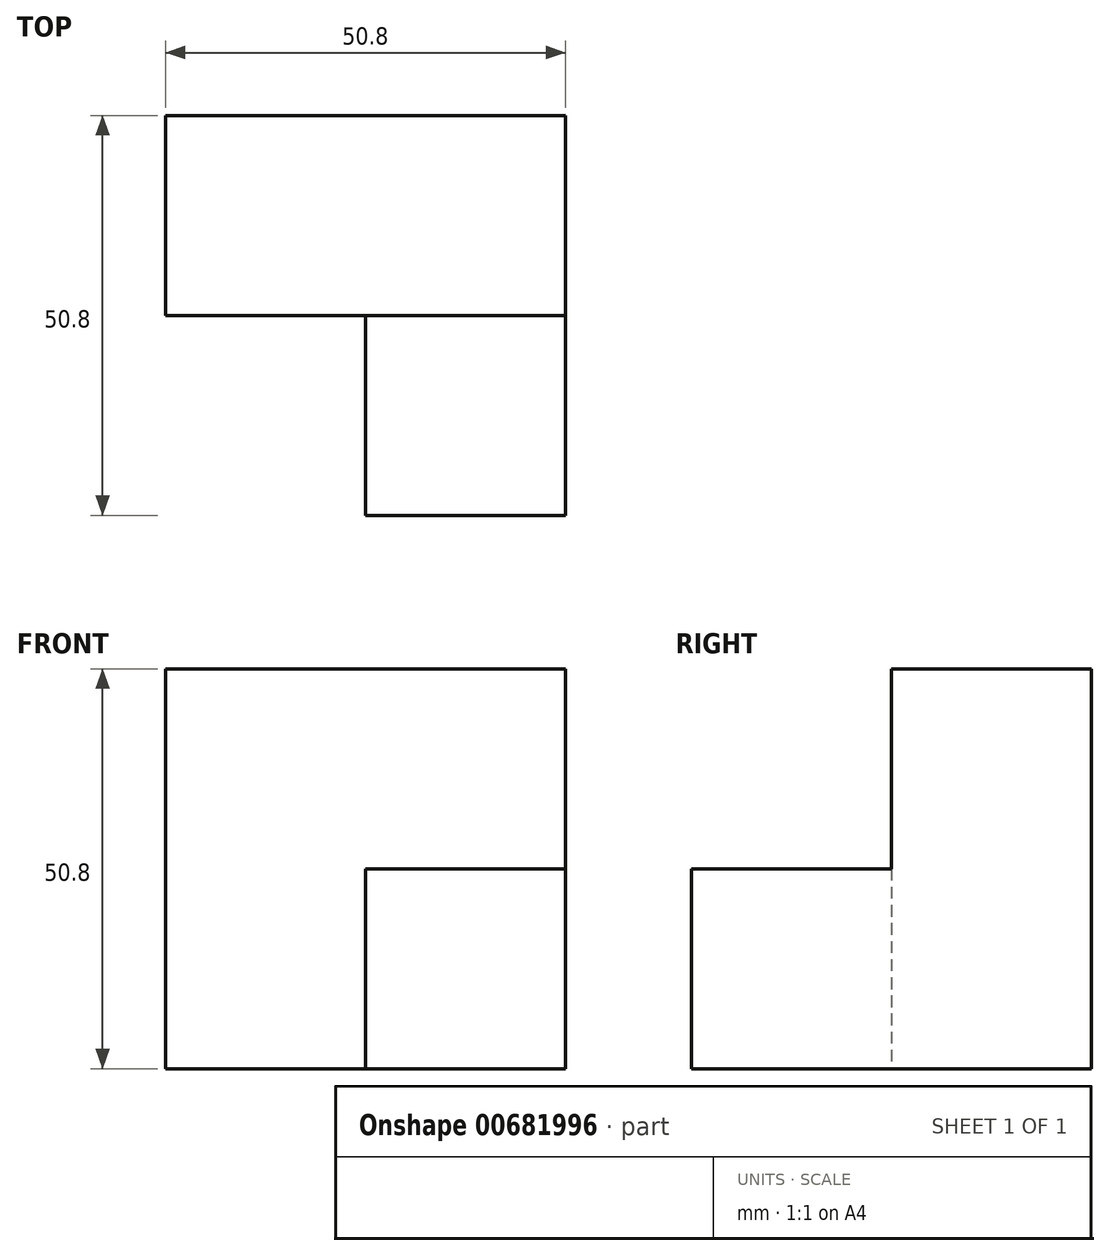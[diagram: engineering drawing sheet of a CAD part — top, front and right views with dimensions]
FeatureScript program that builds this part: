
annotation { "Feature Type Name" : "Feature", "Feature Type Description" : "" }
export const myFeature = defineFeature(function(context is Context, id is Id, definition is map)
    precondition{}
    {
        {
            var Q0;
            Q0=qCreatedBy(makeId("Front.planeOp"),FACE);
            var sketch = newSketch(context, id + "F0", { "sketchPlane" : qUnion([Q0])});
            skLineSegment(sketch, "E0", {"start": v(0, 0) * mm, "end": v(0, 50.8) * mm});
            skLineSegment(sketch, "E1", {"start": v(0, 50.8) * mm, "end": v(-50.8, 50.8) * mm});
            skLineSegment(sketch, "E2", {"start": v(-50.8, 50.8) * mm, "end": v(-50.8, 0) * mm});
            skLineSegment(sketch, "E3", {"start": v(-50.8, 0) * mm, "end": v(0, 0) * mm});
            skSolve(sketch);
        }
        {
            var Q0;
            Q0=makeQuery(id+"F0.imprint","IMPRINT",FACE,{"disambiguationData":[TD([[makeQuery(id+"F0.imprint","IMPRINT",EDGE,{"derivedFrom":sQuery(id+"F0.wireOp",EDGE,"E0")}),1.0]])]});
            extrude(context, id + "F1", {"entities" : qUnion([Q0]), "depth" : 25.4 * mm, "offsetDistance" : 25.4 * mm});
        }
        {
            var Q0;
            Q0=makeQuery(id+"F1.opExtrude","CAP_FACE",FACE,{"disambiguationData":[OSD([sQuery(id+"F0.wireOp",EDGE,"E0"),sQuery(id+"F0.wireOp",EDGE,"E1"),sQuery(id+"F0.wireOp",EDGE,"E2"),sQuery(id+"F0.wireOp",EDGE,"E3")])],"isStart":false});
            var sketch = newSketch(context, id + "F2", { "sketchPlane" : qUnion([Q0])});
            skLineSegment(sketch, "E4", {"start": v(0, 0) * mm, "end": v(0, 25.4) * mm});
            skLineSegment(sketch, "E5", {"start": v(0, 25.4) * mm, "end": v(-25.4, 25.4) * mm});
            skLineSegment(sketch, "E6", {"start": v(-25.4, 25.4) * mm, "end": v(-25.4, 0) * mm});
            skLineSegment(sketch, "E7", {"start": v(-25.4, 0) * mm, "end": v(0, 0) * mm});
            skSolve(sketch);
        }
        {
            var Q0;
            Q0=makeQuery(id+"F2.imprint","IMPRINT",FACE,{"disambiguationData":[TD([[makeQuery(id+"F2.imprint","IMPRINT",EDGE,{"derivedFrom":sQuery(id+"F2.wireOp",EDGE,"E4")}),1.0]])]});
            var sketch = newSketch(context, id + "F3", { "sketchPlane" : qUnion([Q0])});
            skSolve(sketch);
        }
        {
            var Q0;
            Q0 = qSketchRegion(id + "F3", true);
            var Q1;
            Q1=makeQuery(id+"F3.imprint","IMPRINT",FACE,{"disambiguationData":[TD([[makeQuery(id+"F3.imprint","IMPRINT",EDGE,{"derivedFrom":makeQuery(id+"F2.imprint","IMPRINT",EDGE,{"derivedFrom":sQuery(id+"F2.wireOp",EDGE,"E4")})}),1.0]])]});
            extrude(context, id + "F4", {"entities" : qUnion([Q0, Q1]), "operationType" : NewBodyOperationType.ADD, "depth" : 25.4 * mm, "offsetDistance" : 25.4 * mm});
        }
    });
